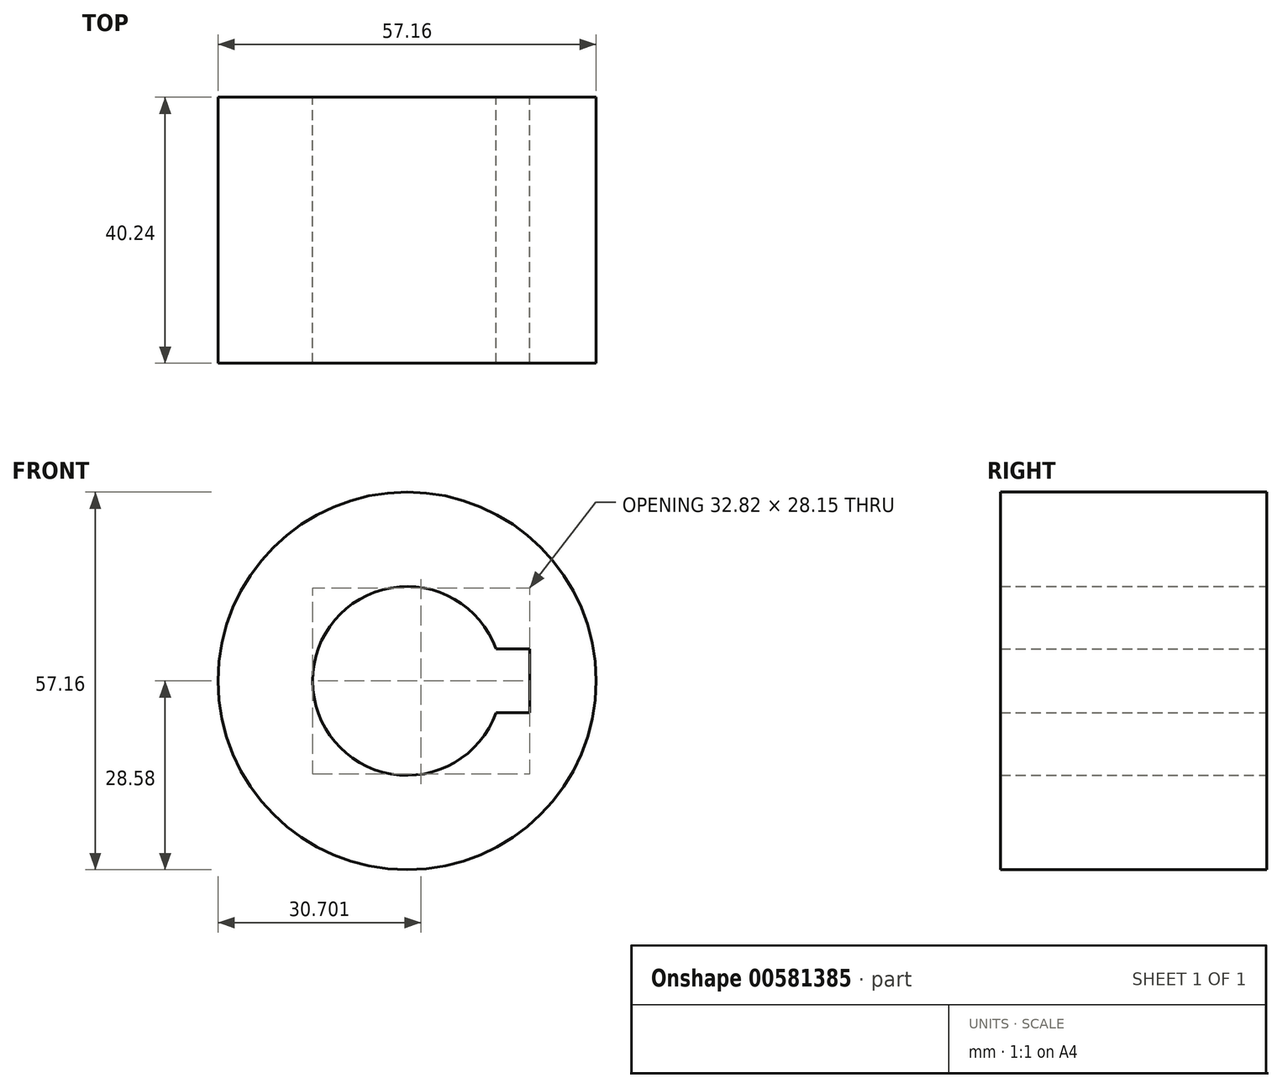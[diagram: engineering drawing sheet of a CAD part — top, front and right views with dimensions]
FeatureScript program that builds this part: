
annotation { "Feature Type Name" : "Feature", "Feature Type Description" : "" }
export const myFeature = defineFeature(function(context is Context, id is Id, definition is map)
    precondition{}
    {
        {
            var Q0;
            Q0=qCreatedBy(makeId("Front.planeOp"),FACE);
            var sketch = newSketch(context, id + "F0", { "sketchPlane" : qUnion([Q0])});
            skCircle(sketch, "E0", {"center": v(0, 0) * mm, "radius": 14.29 * mm});
            skCircle(sketch, "E1", {"center": v(0, 0) * mm, "radius": 28.58 * mm});
            skLineSegment(sketch, "E2", {"start": v(0, 0) * mm, "end": v(53.98, 0) * mm});
            skLineSegment(sketch, "E3", {"start": v(-14.29, 0) * mm, "end": v(18.53, 0) * mm});
            skLineSegment(sketch, "E4", {"start": v(18.53, 0) * mm, "end": v(18.53, -4.83) * mm});
            skLineSegment(sketch, "E5", {"start": v(18.53, 0) * mm, "end": v(18.53, 4.83) * mm});
            skLineSegment(sketch, "E6", {"start": v(18.53, 4.83) * mm, "end": v(13.45, 4.83) * mm});
            skLineSegment(sketch, "E7", {"start": v(18.53, -4.83) * mm, "end": v(13.45, -4.83) * mm});
            skSolve(sketch);
        }
        {
            var Q0;
            Q0=makeQuery(id+"F0.imprint","IMPRINT",FACE,{"disambiguationData":[TD([[makeQuery(id+"F0.imprint","IMPRINT",EDGE,{"derivedFrom":sQuery(id+"F0.wireOp",EDGE,"E1")}),1.0]])]});
            extrude(context, id + "F1", {"entities" : qUnion([Q0]), "endBound" : BoundingType.SYMMETRIC, "depth" : 40.23 * mm, "offsetDistance" : 25.4 * mm});
        }
    });
